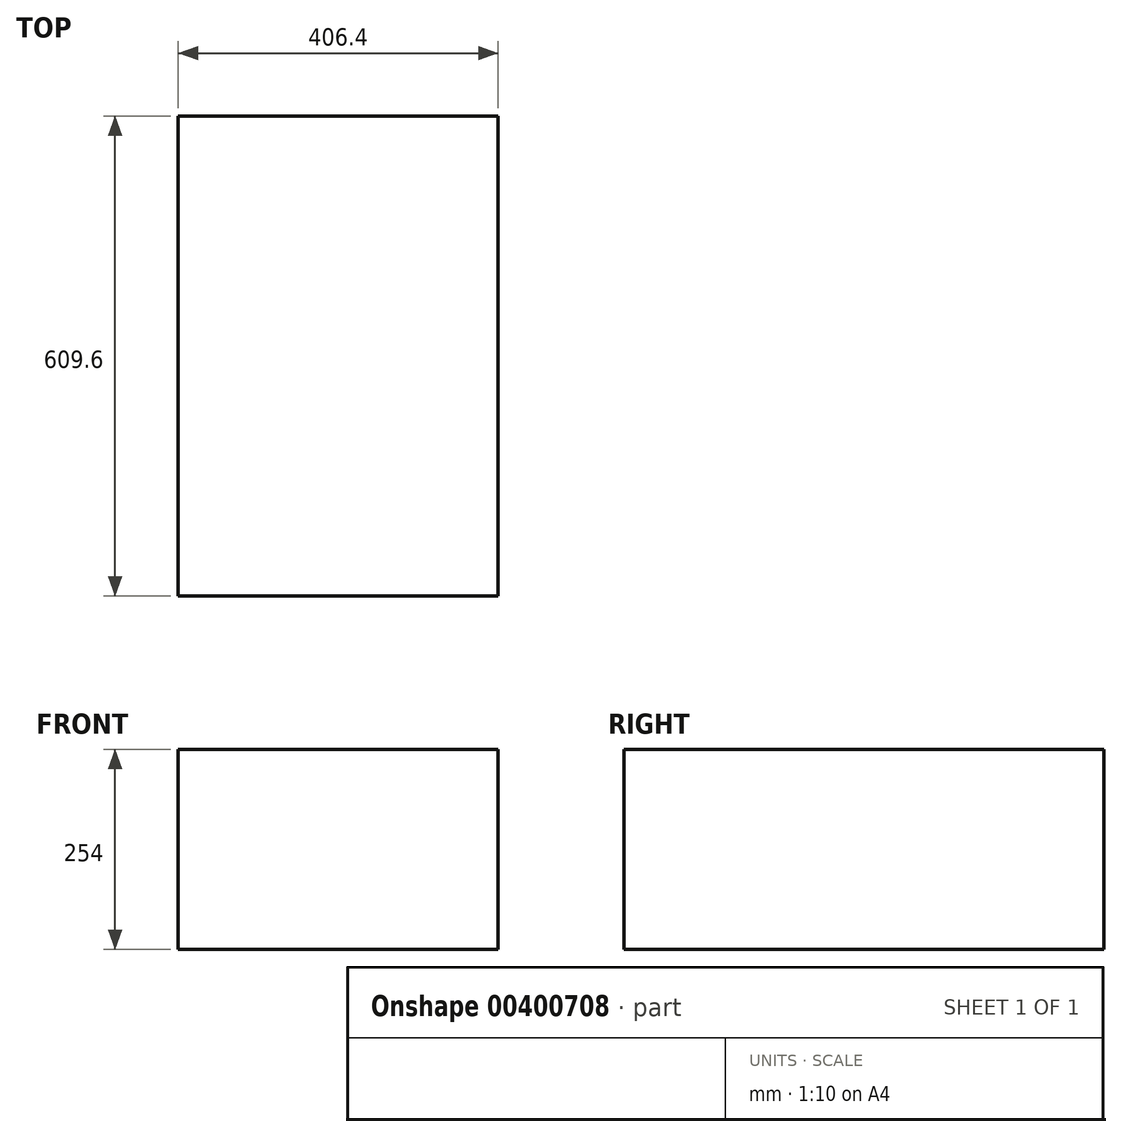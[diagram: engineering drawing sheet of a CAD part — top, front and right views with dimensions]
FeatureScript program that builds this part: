
annotation { "Feature Type Name" : "Feature", "Feature Type Description" : "" }
export const myFeature = defineFeature(function(context is Context, id is Id, definition is map)
    precondition{}
    {
        {
            var Q0;
            Q0=qCreatedBy(makeId("Front.planeOp"),FACE);
            var sketch = newSketch(context, id + "F0", { "sketchPlane" : qUnion([Q0])});
            skLineSegment(sketch, "E0.bottom", {"start": v(0, 0) * mm, "end": v(406.4, 0) * mm});
            skLineSegment(sketch, "E0.top", {"start": v(0, 254) * mm, "end": v(406.4, 254) * mm});
            skLineSegment(sketch, "E0.left", {"start": v(0, 0) * mm, "end": v(0, 254) * mm});
            skLineSegment(sketch, "E0.right", {"start": v(406.4, 0) * mm, "end": v(406.4, 254) * mm});
            skSolve(sketch);
        }
        {
            var Q0;
            Q0 = qSketchRegion(id + "F0", true);
            extrude(context, id + "F1", {"entities" : qUnion([Q0]), "depth" : 609.6 * mm});
        }
    });
